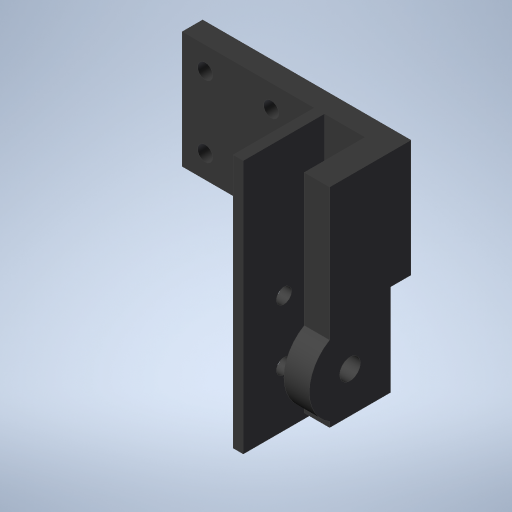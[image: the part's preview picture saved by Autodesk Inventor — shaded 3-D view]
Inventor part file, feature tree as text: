
AUTODESK INVENTOR PART (.ipt)
format: ipt  version: 2024.2 (Build 282272000, 272)  size: 313,856 bytes
history: native  units: mm
features: other x8, extrude x7, sketch x5, reference x4, thread x1, projected_geometry x1
ambient origin geometry x8: Origin, YZ Plane, XZ Plane, XY Plane, X Axis, Y Axis, Z Axis, Center Point
bodies: Body1 (feature_tree)
feature tree (26):
  other  "Твердое тело1"
  other  "РабПлоскость1"
  extrude  "Выдавливание1"  Depth=18.0mm
  sketch  "Эскиз2"
  extrude  "Выдавливание2"  Depth=18.0mm
  extrude  "Выдавливание3"  Depth=14.0mm
  thread  "Резьба1"
  extrude  "Выдавливание4"  Depth=3.0mm
  sketch  "Эскиз4"
  extrude  "Выдавливание5"  Depth=3.0mm
  extrude  "Выдавливание6"  Depth=3.0mm
  extrude  "Выдавливание7"  Depth=3.0mm
  sketch  "Эскиз1"
  reference  "Ссылка1"
  reference  "Ссылка2"
  reference  "Ссылка3"
  reference  "Ссылка4"
  sketch  "Эскиз3"
  sketch  "Эскиз5"
  projected_geometry  "Спроецированная петля2"
  other  "<userpath>\Documents\Artist\3D\Робот.iam"
  other  "Робот.iam"
  other  "боковая стенка:1"
  other  "NEMA17 42-40:2"
  other  "Нижняя крышка:1"
  other  "передняя стенка:2"
